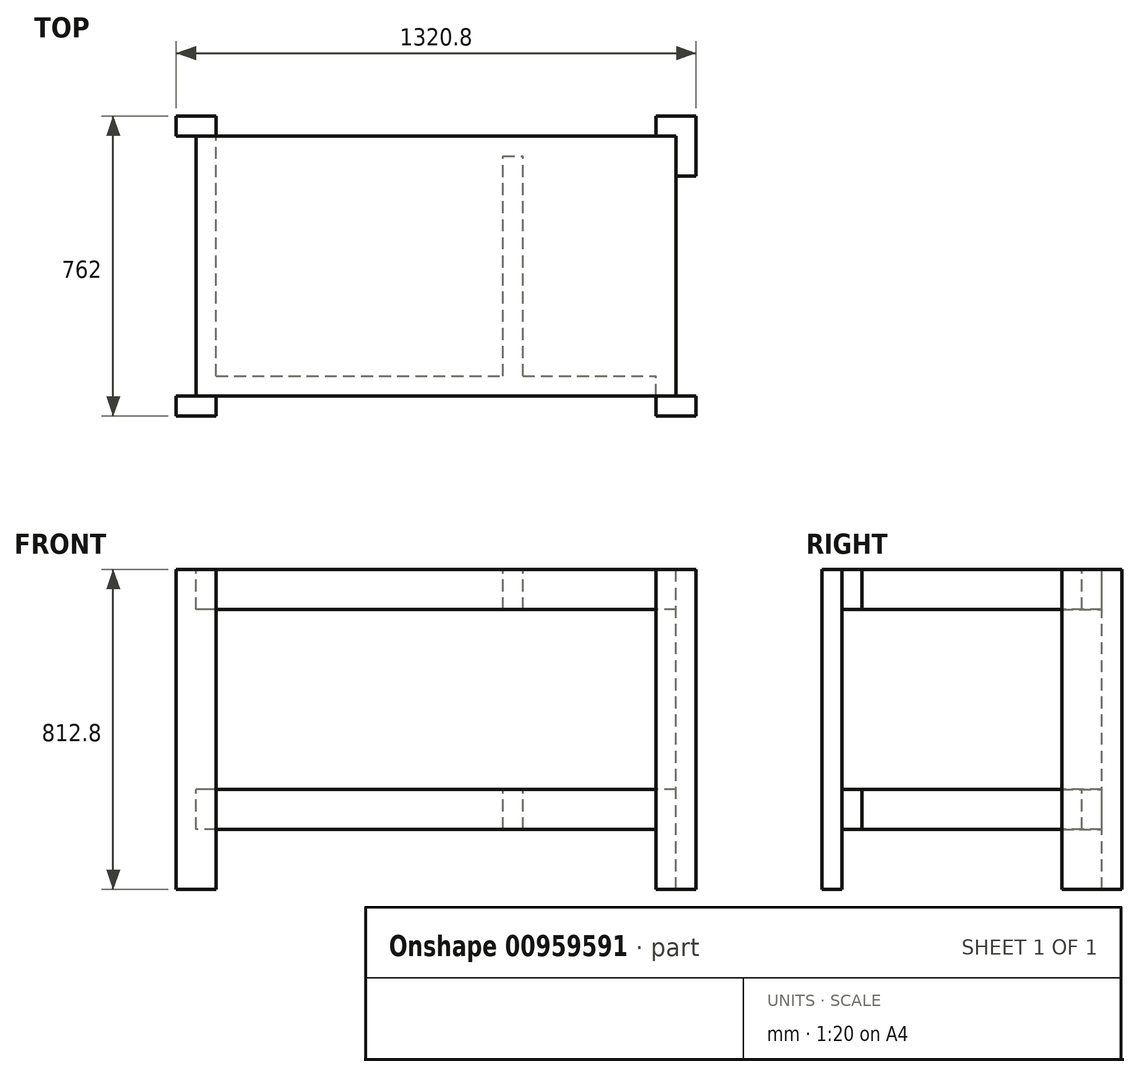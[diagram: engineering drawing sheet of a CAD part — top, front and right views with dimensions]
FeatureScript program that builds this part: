
annotation { "Feature Type Name" : "Feature", "Feature Type Description" : "" }
export const myFeature = defineFeature(function(context is Context, id is Id, definition is map)
    precondition{}
    {
        {
            assignVariable(context, id + "F0", {"name" : "material_thickness", "anyValue" : 3 / 101.6 * mm});
        }
        {
            assignVariable(context, id + "F1", {"name" : "workbench_height", "anyValue" : 812.8 * mm});
        }
        {
            var Q0;
            Q0=qCreatedBy(makeId("Top.planeOp"),FACE);
            var sketch = newSketch(context, id + "F2", { "sketchPlane" : qUnion([Q0])});
            skLineSegment(sketch, "E0.bottom", {"start": v(609.6, 330.2) * mm, "end": v(-609.6, 330.2) * mm});
            skLineSegment(sketch, "E0.top", {"start": v(609.6, -330.2) * mm, "end": v(-609.6, -330.2) * mm});
            skLineSegment(sketch, "E0.left", {"start": v(609.6, 330.2) * mm, "end": v(609.6, -330.2) * mm});
            skLineSegment(sketch, "E0.right", {"start": v(-609.6, 330.2) * mm, "end": v(-609.6, -330.2) * mm});
            skPoint(sketch, "E0.middle", {"position": v(0, 0) * mm});
            skLineSegment(sketch, "E1", {"start": v(0, 330.2) * mm, "end": v(0, -330.2) * mm, "construction": true});
            skLineSegment(sketch, "E2", {"start": v(-609.6, 0) * mm, "end": v(609.6, 0) * mm, "construction": true});
            skLineSegment(sketch, "E3.bottom", {"start": v(660.4, -330.2) * mm, "end": v(558.8, -330.2) * mm});
            skLineSegment(sketch, "E3.top", {"start": v(660.4, -381) * mm, "end": v(558.8, -381) * mm});
            skLineSegment(sketch, "E3.left", {"start": v(660.4, -330.2) * mm, "end": v(660.4, -381) * mm});
            skLineSegment(sketch, "E3.right", {"start": v(558.8, -330.2) * mm, "end": v(558.8, -381) * mm});
            skLineSegment(sketch, "E4.bottom", {"start": v(609.6, -330.2) * mm, "end": v(660.4, -330.2) * mm});
            skLineSegment(sketch, "E4.top", {"start": v(609.6, -228.6) * mm, "end": v(660.4, -228.6) * mm});
            skLineSegment(sketch, "E4.left", {"start": v(609.6, -330.2) * mm, "end": v(609.6, -228.6) * mm});
            skLineSegment(sketch, "E4.right", {"start": v(660.4, -330.2) * mm, "end": v(660.4, -228.6) * mm});
            skLineSegment(sketch, "E5.MirrorCS", {"start": v(558.8, 330.2) * mm, "end": v(558.8, 381) * mm});
            skLineSegment(sketch, "E6.MirrorCS", {"start": v(660.4, 381) * mm, "end": v(558.8, 381) * mm});
            skLineSegment(sketch, "E7.MirrorCS", {"start": v(609.6, 330.2) * mm, "end": v(660.4, 330.2) * mm});
            skLineSegment(sketch, "E8.MirrorCS", {"start": v(660.4, 330.2) * mm, "end": v(660.4, 228.6) * mm});
            skLineSegment(sketch, "E9.MirrorCS", {"start": v(609.6, 330.2) * mm, "end": v(609.6, 228.6) * mm});
            skLineSegment(sketch, "E10.MirrorCS", {"start": v(609.6, 228.6) * mm, "end": v(660.4, 228.6) * mm});
            skLineSegment(sketch, "E11.MirrorCS", {"start": v(-558.8, -330.2) * mm, "end": v(-558.8, -381) * mm});
            skLineSegment(sketch, "E12.MirrorCS", {"start": v(-660.4, -381) * mm, "end": v(-558.8, -381) * mm});
            skLineSegment(sketch, "E13.MirrorCS", {"start": v(-609.6, -330.2) * mm, "end": v(-609.6, -228.6) * mm});
            skLineSegment(sketch, "E14.MirrorCS", {"start": v(-609.6, -330.2) * mm, "end": v(-660.4, -330.2) * mm});
            skLineSegment(sketch, "E15.MirrorCS", {"start": v(-660.4, -330.2) * mm, "end": v(-660.4, -228.6) * mm});
            skLineSegment(sketch, "E16.MirrorCS", {"start": v(-609.6, -228.6) * mm, "end": v(-660.4, -228.6) * mm});
            skLineSegment(sketch, "E17.MirrorCS", {"start": v(-558.8, 330.2) * mm, "end": v(-558.8, 381) * mm});
            skLineSegment(sketch, "E18.MirrorCS", {"start": v(-660.4, 381) * mm, "end": v(-558.8, 381) * mm});
            skLineSegment(sketch, "E19.MirrorCS", {"start": v(-609.6, 330.2) * mm, "end": v(-609.6, 228.6) * mm});
            skLineSegment(sketch, "E20.MirrorCS", {"start": v(-609.6, 330.2) * mm, "end": v(-660.4, 330.2) * mm});
            skLineSegment(sketch, "E21.MirrorCS", {"start": v(-660.4, 330.2) * mm, "end": v(-660.4, 228.6) * mm});
            skLineSegment(sketch, "E22.MirrorCS", {"start": v(-609.6, 228.6) * mm, "end": v(-660.4, 228.6) * mm});
            skLineSegment(sketch, "E23.MirrorCS", {"start": v(660.4, 330.2) * mm, "end": v(660.4, 381) * mm});
            skLineSegment(sketch, "E24.MirrorCS", {"start": v(-660.4, 330.2) * mm, "end": v(-660.4, 381) * mm});
            skLineSegment(sketch, "E25.MirrorCS", {"start": v(-660.4, -330.2) * mm, "end": v(-660.4, -381) * mm});
            skSolve(sketch);
        }
        {
            var Q0;
            Q0=makeQuery(id+"F2.imprint","IMPRINT",FACE,{"disambiguationData":[TD([[makeQuery(id+"F2.imprint","IMPRINT",EDGE,{"derivedFrom":sQuery(id+"F2.wireOp",EDGE,"E19.MirrorCS")}),-1.0]])]});
            var Q1;
            {var subQ1=sQuery(id+"F2.wireOp",EDGE,"E17.MirrorCS");Q1=makeQuery(id+"F2.imprint","IMPRINT",FACE,{"disambiguationData":[TD([[makeQuery(id+"F2.imprint","IMPRINT",EDGE,{"derivedFrom":subQ1}),1.0]])]});}
            var Q2;
            {var subQ1=sQuery(id+"F2.wireOp",EDGE,"E5.MirrorCS");Q2=makeQuery(id+"F2.imprint","IMPRINT",FACE,{"disambiguationData":[TD([[makeQuery(id+"F2.imprint","IMPRINT",EDGE,{"derivedFrom":subQ1}),-1.0]])]});}
            var Q3;
            Q3=makeQuery(id+"F2.imprint","IMPRINT",FACE,{"disambiguationData":[TD([[makeQuery(id+"F2.imprint","IMPRINT",EDGE,{"derivedFrom":sQuery(id+"F2.wireOp",EDGE,"E7.MirrorCS")}),-1.0]])]});
            var Q4;
            Q4=makeQuery(id+"F2.imprint","IMPRINT",FACE,{"disambiguationData":[TD([[makeQuery(id+"F2.imprint","IMPRINT",EDGE,{"derivedFrom":sQuery(id+"F2.wireOp",EDGE,"E4.bottom")}),1.0]])]});
            var Q5;
            Q5=makeQuery(id+"F2.imprint","IMPRINT",FACE,{"disambiguationData":[TD([[makeQuery(id+"F2.imprint","IMPRINT",EDGE,{"derivedFrom":sQuery(id+"F2.wireOp",EDGE,"E3.bottom")}),1.0]])]});
            var Q6;
            Q6=makeQuery(id+"F2.imprint","IMPRINT",FACE,{"disambiguationData":[TD([[makeQuery(id+"F2.imprint","IMPRINT",EDGE,{"derivedFrom":sQuery(id+"F2.wireOp",EDGE,"E13.MirrorCS")}),1.0]])]});
            var Q7;
            {var subQ0=sQuery(id+"F2.wireOp",EDGE,"E11.MirrorCS");Q7=makeQuery(id+"F2.imprint","IMPRINT",FACE,{"disambiguationData":[TD([[makeQuery(id+"F2.imprint","IMPRINT",EDGE,{"derivedFrom":subQ0}),-1.0]])]});}
            extrude(context, id + "F3", {"entities" : qUnion([Q0, Q1, Q2, Q3, Q4, Q5, Q6, Q7]), "oppositeDirection" : true, "depth" : getVariable(context, 'workbench_height'), "offsetDistance" : 25.4 * mm});
        }
        {
            var Q0;
            Q0=makeQuery(id+"F2.imprint","IMPRINT",FACE,{"disambiguationData":[TD([[makeQuery(id+"F2.imprint","IMPRINT",EDGE,{"derivedFrom":sQuery(id+"F2.wireOp",EDGE,"E0.left")}),-1.0]])]});
            extrude(context, id + "F4", {"entities" : qUnion([Q0]), "oppositeDirection" : true, "depth" : getVariable(context, 'material_thickness'), "offsetDistance" : 25.4 * mm});
        }
        {
            var Q0;
            Q0=makeQuery(id+"F4.opExtrude","CAP_FACE",FACE,{"disambiguationData":[OSD([sQuery(id+"F2.wireOp",EDGE,"E0.bottom"),sQuery(id+"F2.wireOp",EDGE,"E0.top"),sQuery(id+"F2.wireOp",EDGE,"E0.left"),sQuery(id+"F2.wireOp",EDGE,"E0.right"),sQuery(id+"F2.wireOp",EDGE,"E3.bottom"),sQuery(id+"F2.wireOp",EDGE,"E4.left"),sQuery(id+"F2.wireOp",EDGE,"E9.MirrorCS"),sQuery(id+"F2.wireOp",EDGE,"E13.MirrorCS"),sQuery(id+"F2.wireOp",EDGE,"E19.MirrorCS")])],"isStart":false});
            var sketch = newSketch(context, id + "F5", { "sketchPlane" : qUnion([Q0])});
            skLineSegment(sketch, "E26.bottom", {"start": v(-609.6, 330.2) * mm, "end": v(-558.8, 330.2) * mm});
            skLineSegment(sketch, "E26.top", {"start": v(-609.6, -330.2) * mm, "end": v(-558.8, -330.2) * mm});
            skLineSegment(sketch, "E26.left", {"start": v(-609.6, 330.2) * mm, "end": v(-609.6, -330.2) * mm});
            skLineSegment(sketch, "E26.right", {"start": v(-558.8, 330.2) * mm, "end": v(-558.8, -330.2) * mm});
            skLineSegment(sketch, "E27", {"start": v(0, 330.2) * mm, "end": v(0, -330.2) * mm, "construction": true});
            skLineSegment(sketch, "E28.MirrorCS", {"start": v(558.8, 330.2) * mm, "end": v(558.8, -330.2) * mm});
            skLineSegment(sketch, "E29.bottom", {"start": v(-558.8, 330.2) * mm, "end": v(558.8, 330.2) * mm});
            skLineSegment(sketch, "E29.top", {"start": v(-558.8, 279.4) * mm, "end": v(558.8, 279.4) * mm});
            skLineSegment(sketch, "E29.left", {"start": v(-558.8, 330.2) * mm, "end": v(-558.8, 279.4) * mm});
            skLineSegment(sketch, "E29.right", {"start": v(558.8, 330.2) * mm, "end": v(558.8, 279.4) * mm});
            skLineSegment(sketch, "E30", {"start": v(-609.6, 0) * mm, "end": v(609.6, 0) * mm, "construction": true});
            skLineSegment(sketch, "E31.MirrorCS", {"start": v(-558.8, -279.4) * mm, "end": v(558.8, -279.4) * mm});
            skLineSegment(sketch, "E32.bottom", {"start": v(-220.13, 279.4) * mm, "end": v(-169.33, 279.4) * mm});
            skLineSegment(sketch, "E32.top", {"start": v(-220.13, -279.4) * mm, "end": v(-169.33, -279.4) * mm});
            skLineSegment(sketch, "E32.left", {"start": v(-220.13, 279.4) * mm, "end": v(-220.13, -279.4) * mm});
            skLineSegment(sketch, "E32.right", {"start": v(-169.33, 279.4) * mm, "end": v(-169.33, -279.4) * mm});
            skLineSegment(sketch, "E33.MirrorCS", {"start": v(169.33, 279.4) * mm, "end": v(169.33, -279.4) * mm});
            skLineSegment(sketch, "E34.MirrorCS", {"start": v(220.13, 279.4) * mm, "end": v(220.13, -279.4) * mm});
            skLineSegment(sketch, "E35", {"start": v(-220.13, 98.97) * mm, "end": v(-558.8, 98.97) * mm, "construction": true});
            skLineSegment(sketch, "E36", {"start": v(-169.33, 100.48) * mm, "end": v(169.33, 100.48) * mm, "construction": true});
            skSolve(sketch);
        }
        {
            var Q0;
            {var subQ2=sQuery(id+"F5.wireOp",EDGE,"E29.right");Q0=makeQuery(id+"F5.imprint","IMPRINT",FACE,{"disambiguationData":[TD([[makeQuery(id+"F5.imprint","IMPRINT",EDGE,{"derivedFrom":subQ2}),1.0]])]});}
            var Q1;
            {var subQ0=sQuery(id+"F5.wireOp",EDGE,"E32.top");Q1=makeQuery(id+"F5.imprint","IMPRINT",FACE,{"disambiguationData":[TD([[makeQuery(id+"F5.imprint","IMPRINT",EDGE,{"derivedFrom":subQ0}),-1.0]])]});}
            var Q2;
            Q2=makeQuery(id+"F5.imprint","IMPRINT",FACE,{"disambiguationData":[TD([[makeQuery(id+"F5.imprint","IMPRINT",EDGE,{"derivedFrom":sQuery(id+"F5.wireOp",EDGE,"E26.bottom")}),1.0]])]});
            var Q3;
            {var subQ0=sQuery(id+"F5.wireOp",EDGE,"E33.MirrorCS");Q3=makeQuery(id+"F5.imprint","IMPRINT",FACE,{"disambiguationData":[TD([[makeQuery(id+"F5.imprint","IMPRINT",EDGE,{"derivedFrom":subQ0}),1.0]])]});}
            var Q4;
            Q4=makeQuery(id+"F5.imprint","IMPRINT",FACE,{"disambiguationData":[TD([[makeQuery(id+"F5.imprint","IMPRINT",EDGE,{"derivedFrom":sQuery(id+"F5.wireOp",EDGE,"E32.bottom")}),-1.0]])]});
            var Q5;
            Q5=makeQuery(id+"F5.imprint","IMPRINT",FACE,{"disambiguationData":[TD([[makeQuery(id+"F5.imprint","IMPRINT",EDGE,{"derivedFrom":sQuery(id+"F5.wireOp",EDGE,"E29.bottom")}),1.0]])]});
            extrude(context, id + "F6", {"entities" : qUnion([Q0, Q1, Q2, Q3, Q4, Q5]), "depth" : 101.6 * mm, "offsetDistance" : 25.4 * mm});
        }
        {
            var Q0;
            Q0=makeQuery(id+"F4.opExtrude","SWEPT_BODY",BODY,{"disambiguationData":[OSD([sQuery(id+"F2.wireOp",EDGE,"E0.bottom"),sQuery(id+"F2.wireOp",EDGE,"E0.top"),sQuery(id+"F2.wireOp",EDGE,"E0.left"),sQuery(id+"F2.wireOp",EDGE,"E0.right"),sQuery(id+"F2.wireOp",EDGE,"E3.bottom"),sQuery(id+"F2.wireOp",EDGE,"E4.left"),sQuery(id+"F2.wireOp",EDGE,"E9.MirrorCS"),sQuery(id+"F2.wireOp",EDGE,"E13.MirrorCS"),sQuery(id+"F2.wireOp",EDGE,"E19.MirrorCS")])]});
            var Q1;
            Q1=qCreatedBy(id+"Fxo05LxyacOpCuS_6.mateConnectorOp",VERTEX);
            var Q2;
            Q2=qCreatedBy(id+"FKw9bP1xuL18fFg_6.mateConnectorOp",VERTEX);
            transform(context, id + "F7", {"entities" : qUnion([Q0]), "transformType" : TransformType.TRANSLATION_3D, "dx" : 0 * mm, "dy" : 0 * mm, "dz" : -(101.6 * mm + getVariable(context, 'material_thickness')), "makeCopy" : true});
        }
        {
            var Q0;
            Q0=makeQuery(id+"F6.opExtrude","SWEPT_BODY",BODY,{"disambiguationData":[OSD([sQuery(id+"F2.wireOp",EDGE,"E0.bottom"),sQuery(id+"F2.wireOp",EDGE,"E0.top"),sQuery(id+"F2.wireOp",EDGE,"E0.left"),sQuery(id+"F2.wireOp",EDGE,"E3.bottom"),sQuery(id+"F2.wireOp",EDGE,"E4.left"),sQuery(id+"F2.wireOp",EDGE,"E9.MirrorCS"),sQuery(id+"F5.wireOp",EDGE,"E26.bottom"),sQuery(id+"F5.wireOp",EDGE,"E26.top"),sQuery(id+"F5.wireOp",EDGE,"E26.left"),sQuery(id+"F5.wireOp",EDGE,"E26.right"),sQuery(id+"F5.wireOp",EDGE,"E28.MirrorCS"),sQuery(id+"F5.wireOp",EDGE,"E29.bottom"),sQuery(id+"F5.wireOp",EDGE,"E29.top"),sQuery(id+"F5.wireOp",EDGE,"E31.MirrorCS"),sQuery(id+"F5.wireOp",EDGE,"E32.left"),sQuery(id+"F5.wireOp",EDGE,"E32.right"),sQuery(id+"F5.wireOp",EDGE,"E33.MirrorCS"),sQuery(id+"F5.wireOp",EDGE,"E34.MirrorCS")])]});
            var Q1;
            Q1=makeQuery(id+"F4.opExtrude","SWEPT_BODY",BODY,{"disambiguationData":[OSD([sQuery(id+"F2.wireOp",EDGE,"E0.bottom"),sQuery(id+"F2.wireOp",EDGE,"E0.top"),sQuery(id+"F2.wireOp",EDGE,"E0.left"),sQuery(id+"F2.wireOp",EDGE,"E0.right"),sQuery(id+"F2.wireOp",EDGE,"E3.bottom"),sQuery(id+"F2.wireOp",EDGE,"E4.left"),sQuery(id+"F2.wireOp",EDGE,"E9.MirrorCS"),sQuery(id+"F2.wireOp",EDGE,"E13.MirrorCS"),sQuery(id+"F2.wireOp",EDGE,"E19.MirrorCS")])]});
            transform(context, id + "F8", {"entities" : qUnion([Q0, Q1]), "transformType" : TransformType.TRANSLATION_3D, "dx" : 0 * mm, "dy" : 0 * mm, "dz" : -558.8 * mm, "makeCopy" : true});
        }
    });
